# Revit family: EKF_EE_РейкаМонтажнаяПерфорированнаяTrivia_AVERES
name_source: partatom
category: Электрооборудование
units: mm (PartAtom-declared; Revit-internal decimal feet)

## family parameters
Всегда вертикально = Нет
На основе рабочей плоскости = Да
Общий = Да
При загрузке вырезать с полостями = Нет
Размер круглого соединителя = Использовать диаметр
Тип детали = Силовой щит
Точка расчета площади = Нет

## types (3) — shared parameters
ADSK_Единица измерения = шт.
ADSK_Завод-изготовитель = EKF
ADSK_Количество = 1
ADSK_Размер_Высота = 36 мм
ADSK_Размер_Глубина = 20 мм
t1 = 2 мм
Высота = 36 мм
Глубина = 20 мм
Изготовитель = EKF
Отступ = 4.6 мм
Серия номенклатуры = Averes
Степень защиты IP = -
ТВ = EKF_2_TRIVIA_AVERES
Тип установки = -
Шаг = 25 мм
zero-valued in all types: ADSK_Масса, Отметка по умолчанию

## per-type parameters (varying)
| type | ADSK_Код изделия | ADSK_Марка | ADSK_Наименование | ADSK_Обозначение | ADSK_Размер_Ширина | КоличествоКв | КоличествоКр | ОтступВырез | Тип | Ширина |
| Рейка монтажная перфорированная Д600 (4шт) EKF AVERES | ARM600 | Рейка монтажная перфорированная Д600 (4 шт) EKF AVERES | Рейка монтажная перфорированная Д600 (4 шт) EKF AVERES | Рейка монтажная перфорированная Д600 (4 шт) EKF AVERES | 498 мм | 20 | 19 | 11.5 мм | 671 мм | 498 мм |
| Рейка монтажная перфорированная Д800 (4шт) EKF AVERES | ARM800 | Рейка монтажная перфорированная Д800 (4 шт) EKF AVERES | Рейка монтажная перфорированная Д800 (4 шт) EKF AVERES | Рейка монтажная перфорированная Д800 (4 шт) EKF AVERES | 698 мм | 28 | 27 | 11.5 мм | 672 мм | 698 мм |
| Рейка монтажная перфорированная Д400 (4шт) EKF AVERES | ARM400 | Рейка монтажная перфорированная Д400 (4 шт) EKF AVERES | Рейка монтажная перфорированная Д400 (4 шт) EKF AVERES | Рейка монтажная перфорированная Д400 (4 шт) EKF AVERES | 297.5 мм | 12 | 11 | 11.25 мм | 670 мм | 297.5 мм |
